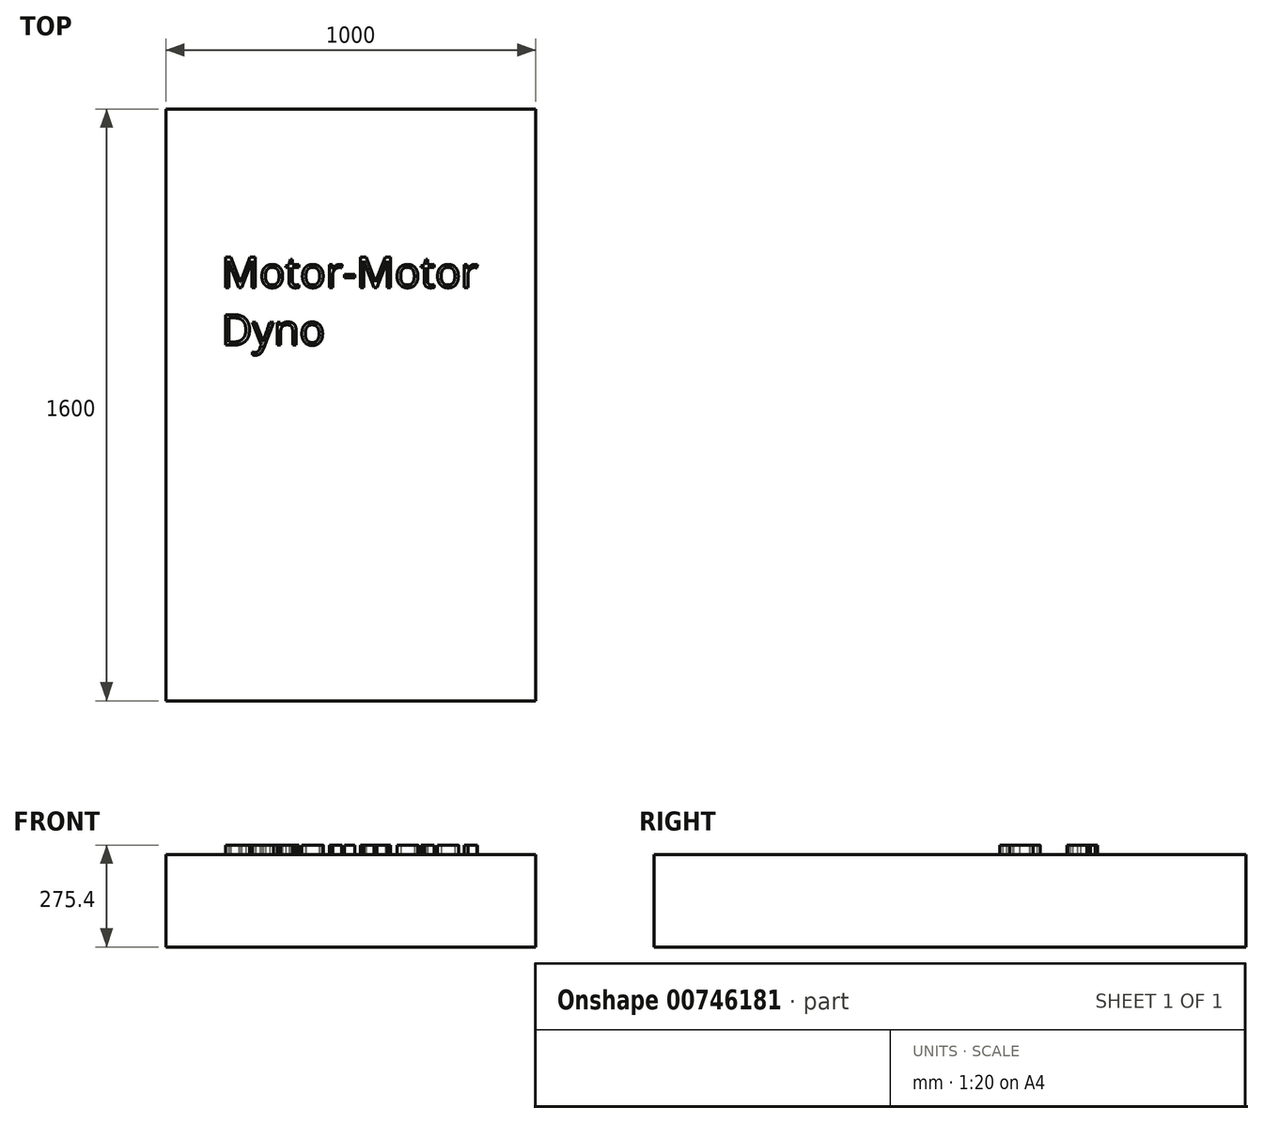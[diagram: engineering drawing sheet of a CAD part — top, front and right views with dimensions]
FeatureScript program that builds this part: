
annotation { "Feature Type Name" : "Feature", "Feature Type Description" : "" }
export const myFeature = defineFeature(function(context is Context, id is Id, definition is map)
    precondition{}
    {
        {
            var Q0;
            Q0=qCreatedBy(makeId("Top.planeOp"),FACE);
            var sketch = newSketch(context, id + "F0", { "sketchPlane" : qUnion([Q0])});
            skLineSegment(sketch, "E0.bottom", {"start": v(500, -800) * mm, "end": v(-500, -800) * mm});
            skLineSegment(sketch, "E0.top", {"start": v(500, 800) * mm, "end": v(-500, 800) * mm});
            skLineSegment(sketch, "E0.left", {"start": v(500, -800) * mm, "end": v(500, 800) * mm});
            skLineSegment(sketch, "E0.right", {"start": v(-500, -800) * mm, "end": v(-500, 800) * mm});
            skPoint(sketch, "E0.middle", {"position": v(0, 0) * mm});
            skSolve(sketch);
        }
        {
            var Q0;
            Q0=makeQuery(id+"F0.imprint","IMPRINT",FACE,{"disambiguationData":[TD([[makeQuery(id+"F0.imprint","IMPRINT",EDGE,{"derivedFrom":sQuery(id+"F0.wireOp",EDGE,"E0.bottom")}),-1.0]])]});
            extrude(context, id + "F1", {"entities" : qUnion([Q0]), "depth" : 250 * mm, "offsetDistance" : 30.48 * mm});
        }
        {
            var Q0;
            Q0=makeQuery(id+"F1.opExtrude","CAP_FACE",FACE,{"disambiguationData":[OSD([sQuery(id+"F0.wireOp",EDGE,"E0.bottom"),sQuery(id+"F0.wireOp",EDGE,"E0.top"),sQuery(id+"F0.wireOp",EDGE,"E0.left"),sQuery(id+"F0.wireOp",EDGE,"E0.right")])],"isStart":false});
            var sketch = newSketch(context, id + "F2", { "sketchPlane" : qUnion([Q0])});
            skText(sketch, "E1", { "text": "Motor-Motor\nDyno", "fontName": "OpenSans-Regular.ttf"});
            const initialGuessF2  = {"E1": [-0.35, 0.3176, 1, 0, 0.0824]};
            skSetInitialGuess(sketch, initialGuessF2);
            skSolve(sketch);
        }
        {
            var Q0;
            Q0 = qSketchRegion(id + "F2", true);
            extrude(context, id + "F3", {"entities" : qUnion([Q0]), "operationType" : NewBodyOperationType.ADD, "depth" : 25.4 * mm, "offsetDistance" : 30.48 * mm});
        }
    });
